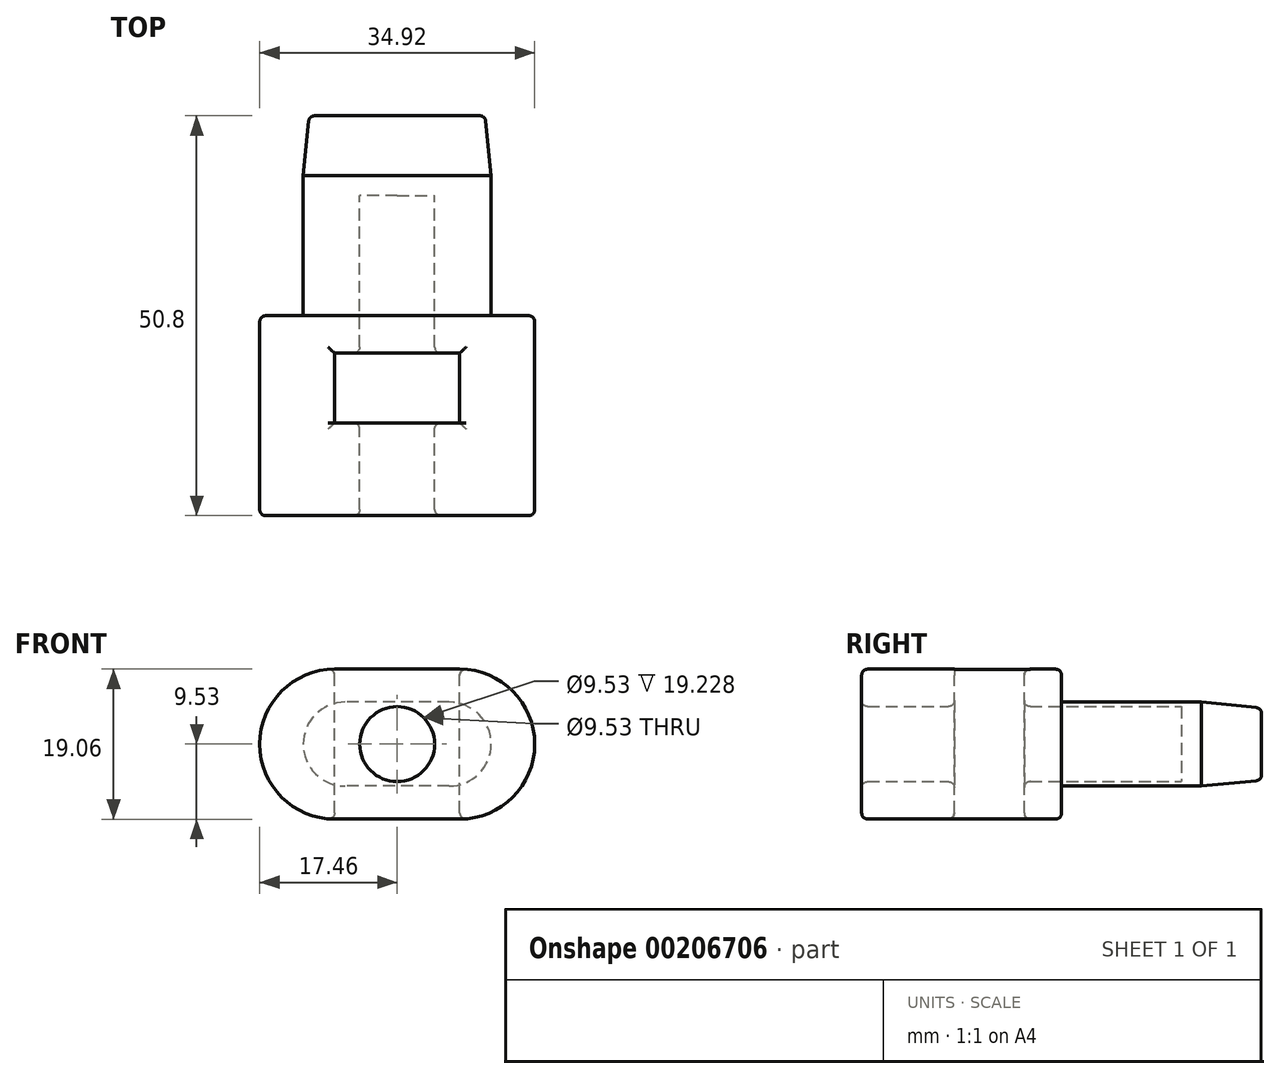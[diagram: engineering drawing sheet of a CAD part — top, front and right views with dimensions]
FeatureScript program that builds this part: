
annotation { "Feature Type Name" : "Feature", "Feature Type Description" : "" }
export const myFeature = defineFeature(function(context is Context, id is Id, definition is map)
    precondition{}
    {
        {
            var Q0;
            Q0=qCreatedBy(makeId("Front.planeOp"),FACE);
            var sketch = newSketch(context, id + "F0", { "sketchPlane" : qUnion([Q0])});
            skLineSegment(sketch, "E0.bottom", {"start": v(7.94, 9.53) * mm, "end": v(-7.94, 9.53) * mm});
            skLineSegment(sketch, "E0.top", {"start": v(7.94, -9.52) * mm, "end": v(-7.94, -9.52) * mm});
            skPoint(sketch, "E0.middle", {"position": v(0, 0) * mm});
            skArc(sketch, "E1", {"start": v(-7.94, 9.53) * mm, "mid": v(-17.46, 0) * mm, "end": v(-7.94, -9.53) * mm});
            skArc(sketch, "E2.MirrorC", {"start": v(7.94, 9.53) * mm, "mid": v(17.46, 0) * mm, "end": v(7.94, -9.53) * mm});
            skPoint(sketch, "E3.orphan", {"position": v(-12.7, 9.52) * mm});
            skPoint(sketch, "E0.right.end.orphan", {"position": v(-20.27, -9.52) * mm});
            skPoint(sketch, "E4.orphan", {"position": v(12.7, -9.52) * mm});
            skPoint(sketch, "E5.orphan", {"position": v(20.27, 9.53) * mm});
            skCircle(sketch, "E6", {"center": v(0, 0) * mm, "radius": 4.76 * mm});
            skSolve(sketch);
        }
        {
            var Q0;
            Q0=makeQuery(id+"F0.imprint","IMPRINT",FACE,{"disambiguationData":[TD([[makeQuery(id+"F0.imprint","IMPRINT",EDGE,{"derivedFrom":sQuery(id+"F0.wireOp",EDGE,"E0.bottom")}),1.0]])]});
            extrude(context, id + "F1", {"entities" : qUnion([Q0]), "depth" : 25.4 * mm});
        }
        {
            var Q0;
            Q0=makeQuery(id+"F1.opExtrude","SWEPT_FACE",FACE,{"disambiguationData":[OSD([sQuery(id+"F0.wireOp",EDGE,"E0.bottom")])]});
            var sketch = newSketch(context, id + "F2", { "sketchPlane" : qUnion([Q0])});
            skLineSegment(sketch, "E7.bottom", {"start": v(7.94, -4.75) * mm, "end": v(-7.94, -4.75) * mm});
            skLineSegment(sketch, "E7.top", {"start": v(7.94, -13.64) * mm, "end": v(-7.94, -13.64) * mm});
            skLineSegment(sketch, "E7.left", {"start": v(7.94, -4.75) * mm, "end": v(7.94, -13.64) * mm});
            skLineSegment(sketch, "E7.right", {"start": v(-7.94, -4.75) * mm, "end": v(-7.94, -13.64) * mm});
            skPoint(sketch, "E7.middle", {"position": v(0, -9.2) * mm});
            skSolve(sketch);
        }
        {
            var Q0;
            Q0=makeQuery(id+"F2.imprint","IMPRINT",FACE,{"disambiguationData":[TD([[makeQuery(id+"F2.imprint","IMPRINT",EDGE,{"derivedFrom":sQuery(id+"F2.wireOp",EDGE,"E7.bottom")}),1.0]])]});
            extrude(context, id + "F3", {"entities" : qUnion([Q0]), "operationType" : NewBodyOperationType.REMOVE, "endBound" : BoundingType.THROUGH_ALL, "oppositeDirection" : true, "depth" : 25.4 * mm});
        }
        {
            var Q0;
            Q0=qCreatedBy(makeId("Front.planeOp"),FACE);
            var sketch = newSketch(context, id + "F4", { "sketchPlane" : qUnion([Q0])});
            skLineSegment(sketch, "E8.bottom", {"start": v(6.6, 5.33) * mm, "end": v(-6.6, 5.33) * mm});
            skLineSegment(sketch, "E8.top", {"start": v(6.6, -5.33) * mm, "end": v(-6.6, -5.33) * mm});
            skPoint(sketch, "E8.middle", {"position": v(0, 0) * mm});
            skArc(sketch, "E9.MirrorC", {"start": v(6.6, 5.33) * mm, "mid": v(11.94, 0) * mm, "end": v(6.6, -5.33) * mm});
            skPoint(sketch, "E10.orphan", {"position": v(-11.35, 5.33) * mm});
            skPoint(sketch, "E8.right.end.orphan", {"position": v(-11.35, -5.33) * mm});
            skPoint(sketch, "E11.orphan", {"position": v(11.35, -5.33) * mm});
            skPoint(sketch, "E12.orphan", {"position": v(11.35, 5.33) * mm});
            skCircle(sketch, "E13", {"center": v(0, 0) * mm, "radius": 4.76 * mm});
            skArc(sketch, "E14.MirrorCS", {"start": v(-6.6, 5.33) * mm, "mid": v(-11.94, 0) * mm, "end": v(-6.6, -5.33) * mm});
            skSolve(sketch);
        }
        {
            var Q0;
            Q0 = qSketchRegion(id + "F4", true);
            extrude(context, id + "F5", {"entities" : qUnion([Q0]), "operationType" : NewBodyOperationType.ADD, "oppositeDirection" : true, "depth" : 25.4 * mm});
        }
        {
            var Q0;
            Q0=makeQuery(id+"F5.opExtrude","CAP_FACE",FACE,{"disambiguationData":[OSD([sQuery(id+"F4.wireOp",EDGE,"E8.bottom"),sQuery(id+"F4.wireOp",EDGE,"E8.top"),sQuery(id+"F4.wireOp",EDGE,"E9.MirrorC"),sQuery(id+"F4.wireOp",EDGE,"E13"),sQuery(id+"F4.wireOp",EDGE,"E14.MirrorCS")])],"isStart":false});
            var sketch = newSketch(context, id + "F6", { "sketchPlane" : qUnion([Q0])});
            skCircle(sketch, "E15", {"center": v(0, 0) * mm, "radius": 4.76 * mm});
            skSolve(sketch);
        }
        {
            var Q0;
            Q0=makeQuery(id+"F6.imprint","IMPRINT",FACE,{"disambiguationData":[TD([[makeQuery(id+"F6.imprint","IMPRINT",EDGE,{"derivedFrom":sQuery(id+"F6.wireOp",EDGE,"E15")}),-1.0]])]});
            extrude(context, id + "F7", {"entities" : qUnion([Q0]), "operationType" : NewBodyOperationType.ADD, "oppositeDirection" : true, "depth" : 10.16 * mm});
        }
        {
            var Q0;
            Q0=makeQuery(id+"F1.opExtrude","CAP_FACE",FACE,{"disambiguationData":[OSD([sQuery(id+"F0.wireOp",EDGE,"E0.bottom"),sQuery(id+"F0.wireOp",EDGE,"E0.top"),sQuery(id+"F0.wireOp",EDGE,"E1"),sQuery(id+"F0.wireOp",EDGE,"E2.MirrorC"),sQuery(id+"F0.wireOp",EDGE,"E6")])],"isStart":false});
            var Q1;
            Q1=makeQuery(id+"F1.opExtrude","CAP_EDGE",EDGE,{"disambiguationData":[OSD([sQuery(id+"F0.wireOp",EDGE,"E2.MirrorC")])],"isStart":true});
            var Q2;
            Q2=makeQuery(id+"F3.boolean.opBoolean","INTERSECT",EDGE,{"derivedFrom":[makeQuery(id+"F1.opExtrude","SWEPT_FACE",FACE,{"disambiguationData":[OSD([sQuery(id+"F0.wireOp",EDGE,"E0.top")])]}),makeQuery(id+"F3.opExtrude","SWEPT_FACE",FACE,{"disambiguationData":[OSD([sQuery(id+"F2.wireOp",EDGE,"E7.top")])]})]});
            var Q3;
            {var subQ0=sQuery(id+"F0.wireOp",EDGE,"E2.MirrorC");var subQ1=sQuery(id+"F0.wireOp",EDGE,"E0.top");Q3=makeQuery(id+"F3.boolean.opBoolean","SPLIT",EDGE,{"disambiguationData":[TD([makeQuery(id+"F1.opExtrude","SWEPT_FACE",FACE,{"disambiguationData":[OSD([subQ1])]}),makeQuery(id+"F1.opExtrude","SWEPT_FACE",FACE,{"disambiguationData":[OSD([subQ0])]}),makeQuery(id+"F3.opExtrude","SWEPT_FACE",FACE,{"disambiguationData":[OSD([sQuery(id+"F2.wireOp",EDGE,"E7.bottom")])]}),makeQuery(id+"F3.opExtrude","SWEPT_FACE",FACE,{"disambiguationData":[OSD([sQuery(id+"F2.wireOp",EDGE,"E7.top")])]}),makeQuery(id+"F3.opExtrude","SWEPT_FACE",FACE,{"disambiguationData":[OSD([sQuery(id+"F2.wireOp",EDGE,"E7.left")])]})])],"derivedFrom":makeQuery(id+"F1.opExtrude","SWEPT_EDGE",EDGE,{"disambiguationData":[OSD([subQ1,subQ0])]})});}
            var Q4;
            {var subQ2=sQuery(id+"F0.wireOp",EDGE,"E0.top");Q4=makeQuery(id+"F3.boolean.opBoolean","SPLIT",FACE,{"disambiguationData":[TD([makeQuery(id+"F3.opExtrude","SWEPT_FACE",FACE,{"disambiguationData":[OSD([sQuery(id+"F2.wireOp",EDGE,"E7.bottom")])]})])],"derivedFrom":makeQuery(id+"F1.opExtrude","SWEPT_FACE",FACE,{"disambiguationData":[OSD([subQ2])]})});}
            var Q5;
            {var subQ0=sQuery(id+"F0.wireOp",EDGE,"E1");var subQ1=sQuery(id+"F0.wireOp",EDGE,"E0.top");Q5=makeQuery(id+"F3.boolean.opBoolean","SPLIT",EDGE,{"disambiguationData":[TD([makeQuery(id+"F1.opExtrude","SWEPT_FACE",FACE,{"disambiguationData":[OSD([subQ1])]}),makeQuery(id+"F1.opExtrude","SWEPT_FACE",FACE,{"disambiguationData":[OSD([subQ0])]}),makeQuery(id+"F3.opExtrude","SWEPT_FACE",FACE,{"disambiguationData":[OSD([sQuery(id+"F2.wireOp",EDGE,"E7.bottom")])]}),makeQuery(id+"F3.opExtrude","SWEPT_FACE",FACE,{"disambiguationData":[OSD([sQuery(id+"F2.wireOp",EDGE,"E7.top")])]}),makeQuery(id+"F3.opExtrude","SWEPT_FACE",FACE,{"disambiguationData":[OSD([sQuery(id+"F2.wireOp",EDGE,"E7.right")])]})])],"derivedFrom":makeQuery(id+"F1.opExtrude","SWEPT_EDGE",EDGE,{"disambiguationData":[OSD([subQ1,subQ0])]})});}
            var Q6;
            Q6=makeQuery(id+"F3.boolean.opBoolean","COPY",EDGE,{"derivedFrom":makeQuery(id+"F3.opExtrude","CAP_EDGE",EDGE,{"disambiguationData":[OSD([sQuery(id+"F2.wireOp",EDGE,"E7.bottom")])],"isStart":true})});
            var Q7;
            Q7=makeQuery(id+"F3.boolean.opBoolean","MERGE",EDGE,{"derivedFrom":[makeQuery(id+"F1.opExtrude","SWEPT_EDGE",EDGE,{"disambiguationData":[OSD([sQuery(id+"F0.wireOp",EDGE,"E0.bottom"),sQuery(id+"F0.wireOp",EDGE,"E1")])]}),makeQuery(id+"F3.opExtrude","CAP_EDGE",EDGE,{"disambiguationData":[OSD([sQuery(id+"F2.wireOp",EDGE,"E7.right")])],"isStart":true})]});
            var Q8;
            Q8=makeQuery(id+"F3.boolean.opBoolean","COPY",EDGE,{"derivedFrom":makeQuery(id+"F3.opExtrude","CAP_EDGE",EDGE,{"disambiguationData":[OSD([sQuery(id+"F2.wireOp",EDGE,"E7.top")])],"isStart":true})});
            var Q9;
            Q9=makeQuery(id+"F3.boolean.opBoolean","MERGE",EDGE,{"derivedFrom":[makeQuery(id+"F1.opExtrude","SWEPT_EDGE",EDGE,{"disambiguationData":[OSD([sQuery(id+"F0.wireOp",EDGE,"E0.bottom"),sQuery(id+"F0.wireOp",EDGE,"E2.MirrorC")])]}),makeQuery(id+"F3.opExtrude","CAP_EDGE",EDGE,{"disambiguationData":[OSD([sQuery(id+"F2.wireOp",EDGE,"E7.left")])],"isStart":true})]});
            var Q10;
            Q10=makeQuery(id+"F3.boolean.opBoolean","INTERSECT",EDGE,{"derivedFrom":[makeQuery(id+"F1.opExtrude","SWEPT_FACE",FACE,{"disambiguationData":[OSD([sQuery(id+"F0.wireOp",EDGE,"E6")])]}),makeQuery(id+"F3.opExtrude","SWEPT_FACE",FACE,{"disambiguationData":[OSD([sQuery(id+"F2.wireOp",EDGE,"E7.bottom")])]})]});
            var Q11;
            Q11=makeQuery(id+"F3.boolean.opBoolean","INTERSECT",EDGE,{"derivedFrom":[makeQuery(id+"F1.opExtrude","SWEPT_FACE",FACE,{"disambiguationData":[OSD([sQuery(id+"F0.wireOp",EDGE,"E6")])]}),makeQuery(id+"F3.opExtrude","SWEPT_FACE",FACE,{"disambiguationData":[OSD([sQuery(id+"F2.wireOp",EDGE,"E7.top")])]})]});
            fillet(context, id + "F8", {"entities" : qUnion([Q0, Q1, Q2, Q3, Q4, Q5, Q6, Q7, Q8, Q9, Q10, Q11]), "radius" : 0.76 * mm, "tangentPropagation" : true, "allowEdgeOverflow" : false});
        }
        {
            var Q0;
            Q0=makeQuery(id+"F7.boolean.opBoolean","MERGE",FACE,{"derivedFrom":[makeQuery(id+"F5.opExtrude","CAP_FACE",FACE,{"disambiguationData":[OSD([sQuery(id+"F4.wireOp",EDGE,"E8.bottom"),sQuery(id+"F4.wireOp",EDGE,"E8.top"),sQuery(id+"F4.wireOp",EDGE,"E9.MirrorC"),sQuery(id+"F4.wireOp",EDGE,"E13"),sQuery(id+"F4.wireOp",EDGE,"E14.MirrorCS")])],"isStart":false}),makeQuery(id+"F7.opExtrude","CAP_FACE",FACE,{"disambiguationData":[OSD([sQuery(id+"F6.wireOp",EDGE,"E15")])],"isStart":true})]});
            chamfer(context, id + "F9", {"entities" : qUnion([Q0]), "chamferType" : ChamferType.TWO_OFFSETS, "width1" : 0.76 * mm, "oppositeDirection" : true, "width2" : 7.62 * mm, "tangentPropagation" : true});
        }
        {
            var Q0;
            Q0=makeQuery(id+"F7.boolean.opBoolean","MERGE",FACE,{"derivedFrom":[makeQuery(id+"F5.opExtrude","CAP_FACE",FACE,{"disambiguationData":[OSD([sQuery(id+"F4.wireOp",EDGE,"E8.bottom"),sQuery(id+"F4.wireOp",EDGE,"E8.top"),sQuery(id+"F4.wireOp",EDGE,"E9.MirrorC"),sQuery(id+"F4.wireOp",EDGE,"E13"),sQuery(id+"F4.wireOp",EDGE,"E14.MirrorCS")])],"isStart":false}),makeQuery(id+"F7.opExtrude","CAP_FACE",FACE,{"disambiguationData":[OSD([sQuery(id+"F6.wireOp",EDGE,"E15")])],"isStart":true})]});
            fillet(context, id + "F10", {"entities" : qUnion([Q0]), "radius" : 0.76 * mm, "tangentPropagation" : true, "allowEdgeOverflow" : false});
        }
    });
